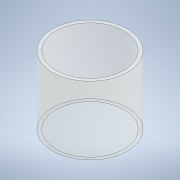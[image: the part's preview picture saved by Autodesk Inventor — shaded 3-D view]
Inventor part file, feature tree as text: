
AUTODESK INVENTOR PART (.ipt)
format: ipt  version: 2020 (Build 240168000, 168)  size: 102,912 bytes
history: native  units: mm
features: other x1, extrude x1, sketch x1
ambient origin geometry x8: Origin, YZ Plane, XZ Plane, XY Plane, X Axis, Y Axis, Z Axis, Center Point
bodies: Body1 (feature_tree)
feature tree (3):
  other  "Твердое тело1"
  extrude  "Выдавливание1"  Depth=40.0mm
  sketch  "Эскиз1"
